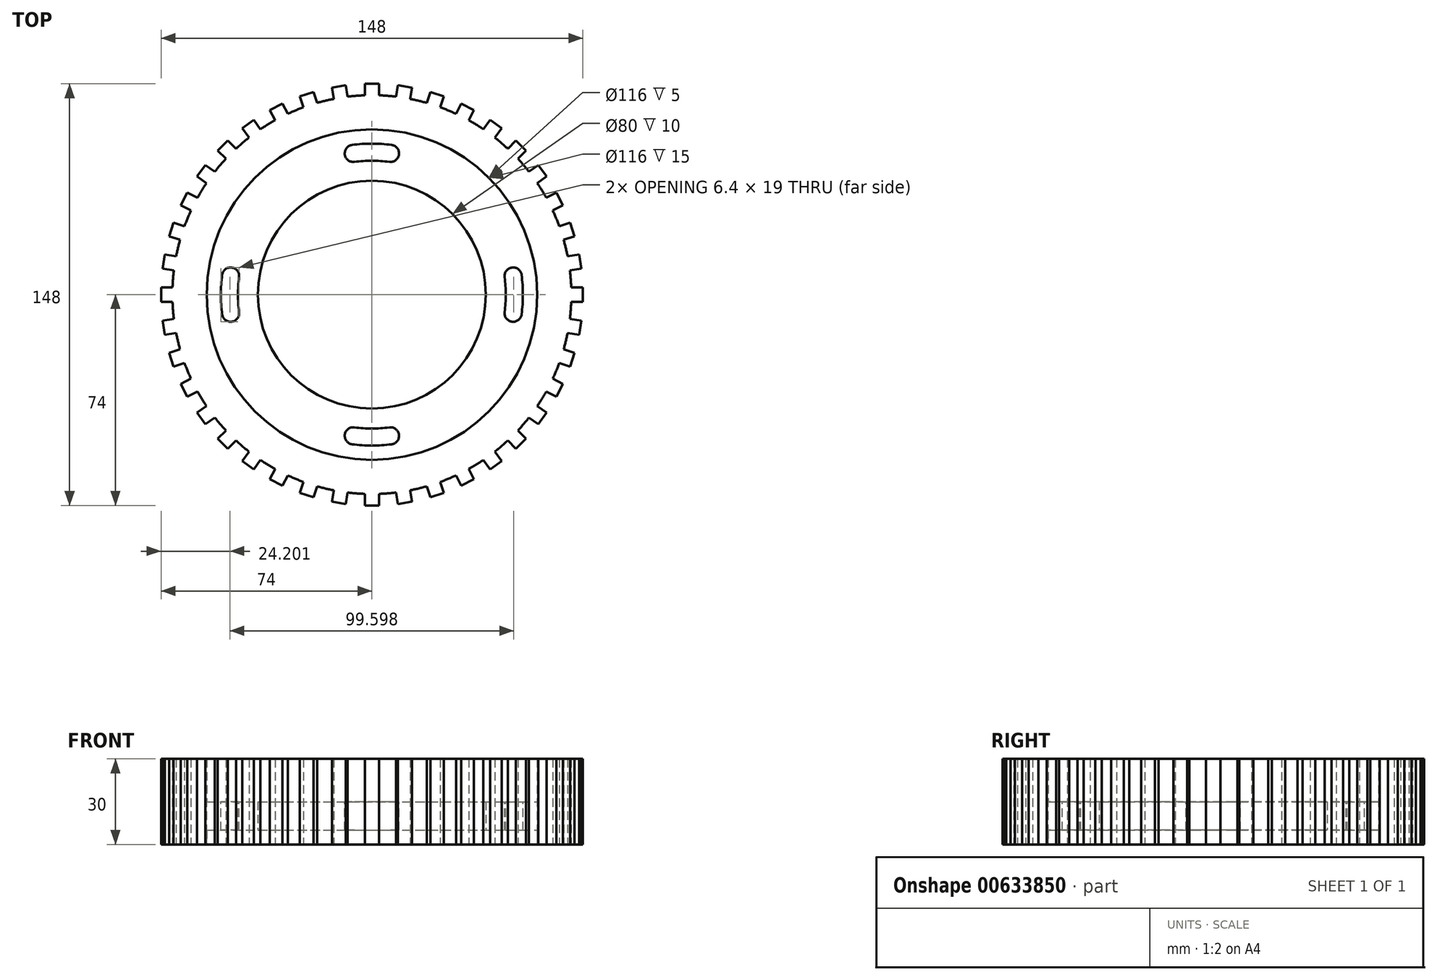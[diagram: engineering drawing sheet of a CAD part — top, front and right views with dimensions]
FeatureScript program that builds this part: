
annotation { "Feature Type Name" : "Feature", "Feature Type Description" : "" }
export const myFeature = defineFeature(function(context is Context, id is Id, definition is map)
    precondition{}
    {
        {
            var Q0;
            Q0=qCreatedBy(makeId("Right.planeOp"),FACE);
            var sketch = newSketch(context, id + "F0", { "sketchPlane" : qUnion([Q0])});
            skLineSegment(sketch, "E0", {"start": v(-70, 0) * mm, "end": v(-70, 30) * mm});
            skLineSegment(sketch, "E1", {"start": v(-70, 30) * mm, "end": v(-58, 30) * mm});
            skLineSegment(sketch, "E2", {"start": v(-58, 30) * mm, "end": v(-58, 15) * mm});
            skLineSegment(sketch, "E3", {"start": v(-58, 15) * mm, "end": v(-40, 15) * mm});
            skLineSegment(sketch, "E4", {"start": v(-40, 15) * mm, "end": v(-40, 5) * mm});
            skLineSegment(sketch, "E5", {"start": v(-40, 5) * mm, "end": v(-58, 5) * mm});
            skLineSegment(sketch, "E6", {"start": v(-58, 5) * mm, "end": v(-58, 0) * mm});
            skLineSegment(sketch, "E7", {"start": v(-58, 0) * mm, "end": v(-70, 0) * mm});
            skLineSegment(sketch, "E8", {"start": v(0, 0) * mm, "end": v(0, 38.77) * mm, "construction": true});
            skLineSegment(sketch, "E9", {"start": v(-70, 15) * mm, "end": v(0, 15) * mm, "construction": true});
            skSolve(sketch);
        }
        {
            var Q0;
            Q0=makeQuery(id+"F0.imprint","IMPRINT",FACE,{"disambiguationData":[TD([[makeQuery(id+"F0.imprint","IMPRINT",EDGE,{"derivedFrom":sQuery(id+"F0.wireOp",EDGE,"E0")}),-1.0]])]});
            var Q1;
            Q1=sQuery(id+"F0.wireOp",EDGE,"E8");
            revolve(context, id + "F1", {"entities" : qUnion([Q0]), "axis" : qUnion([Q1]), "revolveType" : RevolveType.FULL});
        }
        {
            var Q0;
            Q0=qCreatedBy(makeId("Top.planeOp"),FACE);
            var sketch = newSketch(context, id + "F2", { "sketchPlane" : qUnion([Q0])});
            skLineSegment(sketch, "E10.bottom", {"start": v(-65, -2.5) * mm, "end": v(-74, -2.5) * mm});
            skLineSegment(sketch, "E10.top", {"start": v(-65, 2.5) * mm, "end": v(-74, 2.5) * mm});
            skLineSegment(sketch, "E10.left", {"start": v(-65, -2.5) * mm, "end": v(-65, 2.5) * mm});
            skLineSegment(sketch, "E10.right", {"start": v(-74, -2.5) * mm, "end": v(-74, 2.5) * mm});
            skLineSegment(sketch, "E11", {"start": v(-65, 0) * mm, "end": v(0, 0) * mm, "construction": true});
            skSolve(sketch);
        }
        {
            var Q0;
            Q0 = qSketchRegion(id + "F2", true);
            var Q1;
            Q1=makeQuery(id+"F1.opRevolve","SWEPT_FACE",FACE,{"disambiguationData":[OSD([sQuery(id+"F0.wireOp",EDGE,"E1")])]});
            extrude(context, id + "F3", {"entities" : qUnion([Q0]), "operationType" : NewBodyOperationType.ADD, "endBound" : BoundingType.UP_TO_SURFACE, "depth" : 25 * mm, "endBoundEntityFace" : qUnion([Q1]), "offsetDistance" : 25 * mm});
        }
        {
            var Q0;
            Q0=makeQuery(id+"F1.opRevolve","SWEPT_BODY",BODY,{"disambiguationData":[OSD([sQuery(id+"F0.wireOp",EDGE,"E0"),sQuery(id+"F0.wireOp",EDGE,"E1"),sQuery(id+"F0.wireOp",EDGE,"E2"),sQuery(id+"F0.wireOp",EDGE,"E3"),sQuery(id+"F0.wireOp",EDGE,"E4"),sQuery(id+"F0.wireOp",EDGE,"E5"),sQuery(id+"F0.wireOp",EDGE,"E6"),sQuery(id+"F0.wireOp",EDGE,"E7")])]});
            var Q1;
            Q1=makeQuery(id+"F1.opRevolve","SWEPT_FACE",FACE,{"disambiguationData":[OSD([sQuery(id+"F0.wireOp",EDGE,"E0")])]});
            circularPattern(context, id + "F4", {"operationType" : NewBodyOperationType.ADD, "entities" : qUnion([Q0]), "axis" : qUnion([Q1]), "angle" : 360 * degree, "instanceCount" : 40, "equalSpace" : true});
        }
        {
            var Q0;
            Q0=makeQuery(id+"F1.opRevolve","SWEPT_FACE",FACE,{"disambiguationData":[OSD([sQuery(id+"F0.wireOp",EDGE,"E3")])]});
            var sketch = newSketch(context, id + "F5", { "sketchPlane" : qUnion([Q0])});
            skArc(sketch, "E12", {"start": v(-49.57, 6.53) * mm, "mid": v(-50, 0) * mm, "end": v(-49.57, -6.53) * mm, "construction": true});
            skArc(sketch, "E13.0.startCap", {"start": v(-52.55, 6.92) * mm, "mid": v(-49.18, 9.5) * mm, "end": v(-46.6, 6.13) * mm});
            skArc(sketch, "E13.0.endCap", {"start": v(-46.6, -6.13) * mm, "mid": v(-49.18, -9.5) * mm, "end": v(-52.55, -6.92) * mm});
            skArc(sketch, "E13.0.left", {"start": v(-46.6, 6.13) * mm, "mid": v(-47, 0) * mm, "end": v(-46.6, -6.13) * mm});
            skArc(sketch, "E13.0.right", {"start": v(-52.55, 6.92) * mm, "mid": v(-53, 0) * mm, "end": v(-52.55, -6.92) * mm});
            skLineSegment(sketch, "E14", {"start": v(-49.57, -6.53) * mm, "end": v(0, 0) * mm, "construction": true});
            skLineSegment(sketch, "E15", {"start": v(-49.57, 6.53) * mm, "end": v(0, 0) * mm, "construction": true});
            skLineSegment(sketch, "E16", {"start": v(0, 0) * mm, "end": v(-83.86, 0) * mm, "construction": true});
            skArc(sketch, "E17.1.0", {"start": v(6.92, 52.55) * mm, "mid": v(0, 53) * mm, "end": v(-6.92, 52.55) * mm});
            skArc(sketch, "E17.1.1", {"start": v(6.13, 46.6) * mm, "mid": v(0, 47) * mm, "end": v(-6.13, 46.6) * mm});
            skArc(sketch, "E17.1.2", {"start": v(-6.13, 46.6) * mm, "mid": v(-9.5, 49.18) * mm, "end": v(-6.92, 52.55) * mm});
            skArc(sketch, "E17.1.3", {"start": v(6.92, 52.55) * mm, "mid": v(9.5, 49.18) * mm, "end": v(6.13, 46.6) * mm});
            skArc(sketch, "E17.1.4", {"start": v(6.53, 49.57) * mm, "mid": v(0, 50) * mm, "end": v(-6.53, 49.57) * mm, "construction": true});
            skArc(sketch, "E17.2.0", {"start": v(52.55, -6.92) * mm, "mid": v(53, 0) * mm, "end": v(52.55, 6.92) * mm});
            skArc(sketch, "E17.2.1", {"start": v(46.6, -6.13) * mm, "mid": v(47, 0) * mm, "end": v(46.6, 6.13) * mm});
            skArc(sketch, "E17.2.2", {"start": v(46.6, 6.13) * mm, "mid": v(49.18, 9.5) * mm, "end": v(52.55, 6.92) * mm});
            skArc(sketch, "E17.2.3", {"start": v(52.55, -6.92) * mm, "mid": v(49.18, -9.5) * mm, "end": v(46.6, -6.13) * mm});
            skArc(sketch, "E17.2.4", {"start": v(49.57, -6.53) * mm, "mid": v(50, 0) * mm, "end": v(49.57, 6.53) * mm, "construction": true});
            skArc(sketch, "E17.3.0", {"start": v(-6.92, -52.55) * mm, "mid": v(0, -53) * mm, "end": v(6.92, -52.55) * mm});
            skArc(sketch, "E17.3.1", {"start": v(-6.13, -46.6) * mm, "mid": v(0, -47) * mm, "end": v(6.13, -46.6) * mm});
            skArc(sketch, "E17.3.2", {"start": v(6.13, -46.6) * mm, "mid": v(9.5, -49.18) * mm, "end": v(6.92, -52.55) * mm});
            skArc(sketch, "E17.3.3", {"start": v(-6.92, -52.55) * mm, "mid": v(-9.5, -49.18) * mm, "end": v(-6.13, -46.6) * mm});
            skArc(sketch, "E17.3.4", {"start": v(-6.53, -49.57) * mm, "mid": v(0, -50) * mm, "end": v(6.53, -49.57) * mm, "construction": true});
            skLineSegment(sketch, "E17.anchor1", {"start": v(0, 0) * mm, "end": v(-52.55, -6.92) * mm, "construction": true});
            skLineSegment(sketch, "E17.anchor2", {"start": v(0, 0) * mm, "end": v(-52.55, -6.92) * mm, "construction": true});
            skSolve(sketch);
        }
        {
            var Q0;
            Q0 = qSketchRegion(id + "F5", true);
            extrude(context, id + "F6", {"entities" : qUnion([Q0]), "operationType" : NewBodyOperationType.REMOVE, "endBound" : BoundingType.THROUGH_ALL, "oppositeDirection" : true, "depth" : 25 * mm, "offsetDistance" : 25 * mm});
        }
    });
